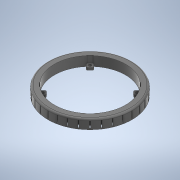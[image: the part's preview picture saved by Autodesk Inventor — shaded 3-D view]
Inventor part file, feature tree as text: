
AUTODESK INVENTOR PART (.ipt)
format: ipt  version: 2020 (Build 240168000, 168)  size: 917,504 bytes
history: native  units: mm
features: extrude x7, projected_geometry x7, sketch x6, pattern_circular x4, fillet x3, other x1
ambient origin geometry x8: Origin, YZ Plane, XZ Plane, XY Plane, X Axis, Y Axis, Z Axis, Center Point
bodies: Body1 (feature_tree)
feature tree (28):
  other  "Твердое тело1"
  sketch  "Эскиз1"
  extrude  "Выдавливание1"  Depth=88.0mm
  extrude  "Выдавливание2"  Depth=5.7mm
  pattern_circular  "Круговой массив1"  [2 undecoded]
  extrude  "Выдавливание3"  Depth=5.4mm
  fillet  "Сопряжение1"  Radius=98.0mm
  extrude  "Выдавливание4"  Depth=84.0mm
  pattern_circular  "Круговой массив2"  [2 undecoded]
  fillet  "Сопряжение2"  Radius=98.0mm
  extrude  "Выдавливание5"  Depth=84.0mm
  pattern_circular  "Круговой массив3"  [2 undecoded]
  extrude  "Выдавливание6"  Depth=10.0mm TaperAngle=0.0deg
  fillet  "Сопряжение3"  Radius=320.0mm
  sketch  "Эскиз6"
  extrude  "Выдавливание7"  Depth=2.0mm
  pattern_circular  "Круговой массив4"  [2 undecoded]
  sketch  "Эскиз2"
  sketch  "Эскиз3"
  projected_geometry  "Спроецированная петля1"
  sketch  "Эскиз4"
  projected_geometry  "Спроецированная петля2"
  sketch  "Эскиз5"
  projected_geometry  "Спроецированная петля3"
  projected_geometry  "Спроецированная петля4"
  projected_geometry  "Спроецированная петля5"
  projected_geometry  "Спроецированная петля6"
  projected_geometry  "Спроецированная петля7"
note: 8 required parameter values undecoded (feature->parameter linkage not recoverable at this tier; creation-order binding heuristic only, values carry confidence <= 0.55)
